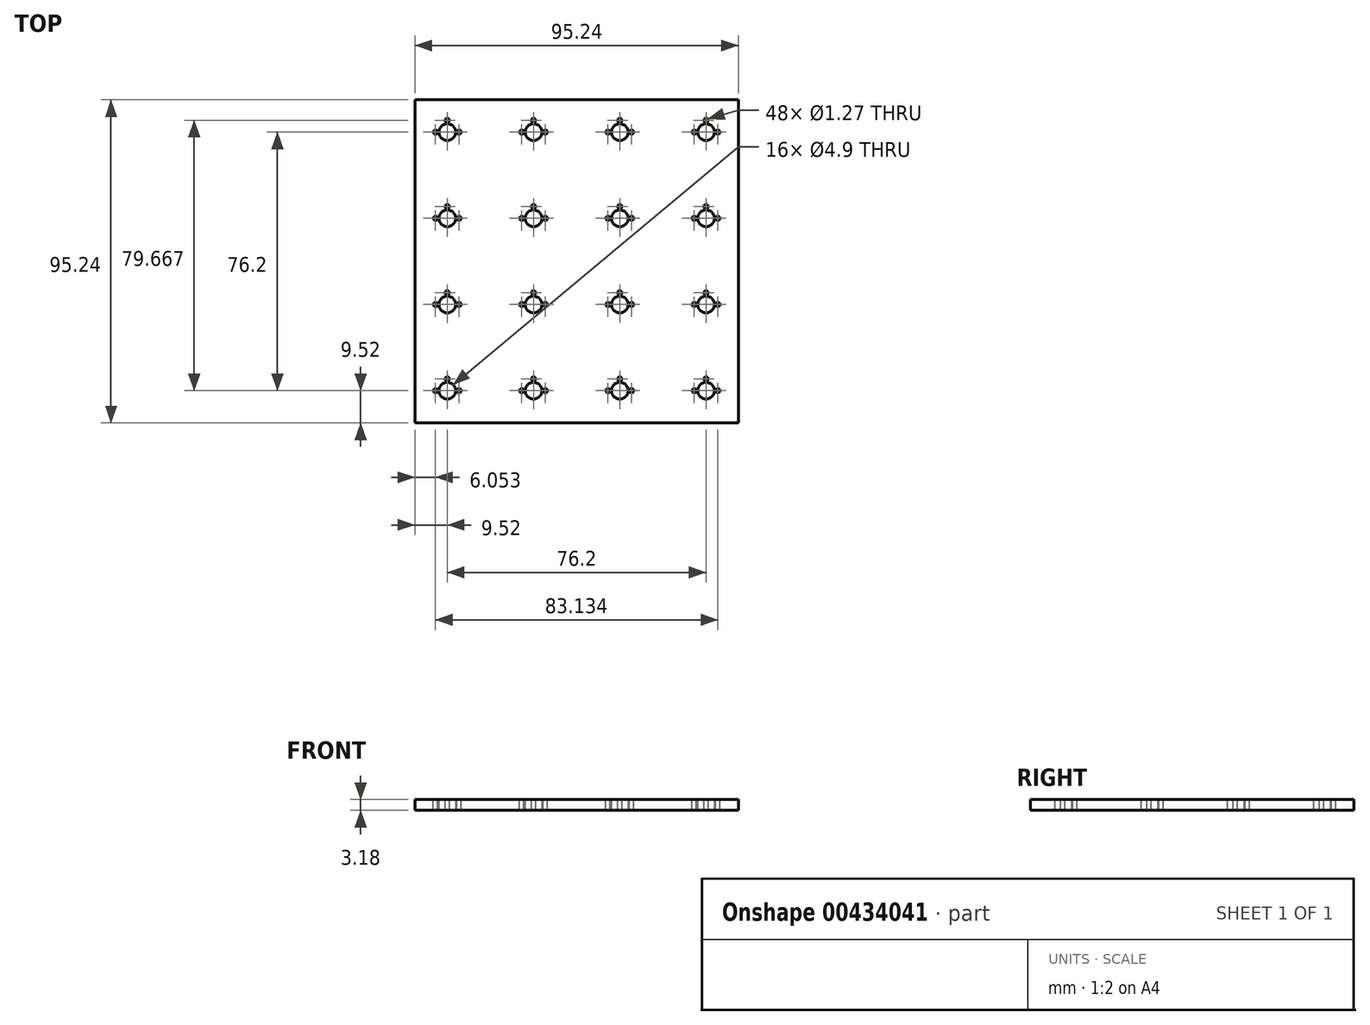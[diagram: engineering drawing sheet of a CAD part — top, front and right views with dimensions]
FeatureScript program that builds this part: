
annotation { "Feature Type Name" : "Feature", "Feature Type Description" : "" }
export const myFeature = defineFeature(function(context is Context, id is Id, definition is map)
    precondition{}
    {
        {
            var Q0;
            Q0=qCreatedBy(makeId("Top.planeOp"),FACE);
            var sketch = newSketch(context, id + "F0", { "sketchPlane" : qUnion([Q0])});
            skLineSegment(sketch, "E0.bottom", {"start": v(47.63, 47.62) * mm, "end": v(-47.62, 47.62) * mm});
            skLineSegment(sketch, "E0.top", {"start": v(47.62, -47.63) * mm, "end": v(-47.63, -47.63) * mm});
            skLineSegment(sketch, "E0.left", {"start": v(47.63, 47.62) * mm, "end": v(47.63, -47.63) * mm});
            skLineSegment(sketch, "E0.right", {"start": v(-47.63, 47.62) * mm, "end": v(-47.63, -47.62) * mm});
            skPoint(sketch, "E0.middle", {"position": v(0, 0) * mm});
            skCircle(sketch, "E1", {"center": v(-38.1, 38.1) * mm, "radius": 2.45 * mm});
            skCircle(sketch, "E2.0.1.0", {"center": v(-38.1, 12.7) * mm, "radius": 2.45 * mm});
            skCircle(sketch, "E2.0.2.0", {"center": v(-38.1, -12.7) * mm, "radius": 2.45 * mm});
            skCircle(sketch, "E2.0.3.0", {"center": v(-38.1, -38.1) * mm, "radius": 2.45 * mm});
            skCircle(sketch, "E2.1.0.0", {"center": v(-12.7, 38.1) * mm, "radius": 2.45 * mm});
            skCircle(sketch, "E2.1.1.0", {"center": v(-12.7, 12.7) * mm, "radius": 2.45 * mm});
            skCircle(sketch, "E2.1.2.0", {"center": v(-12.7, -12.7) * mm, "radius": 2.45 * mm});
            skCircle(sketch, "E2.1.3.0", {"center": v(-12.7, -38.1) * mm, "radius": 2.45 * mm});
            skCircle(sketch, "E2.2.0.0", {"center": v(12.7, 38.1) * mm, "radius": 2.45 * mm});
            skCircle(sketch, "E2.2.1.0", {"center": v(12.7, 12.7) * mm, "radius": 2.45 * mm});
            skCircle(sketch, "E2.2.2.0", {"center": v(12.7, -12.7) * mm, "radius": 2.45 * mm});
            skCircle(sketch, "E2.2.3.0", {"center": v(12.7, -38.1) * mm, "radius": 2.45 * mm});
            skCircle(sketch, "E2.3.0.0", {"center": v(38.1, 38.1) * mm, "radius": 2.45 * mm});
            skCircle(sketch, "E2.3.1.0", {"center": v(38.1, 12.7) * mm, "radius": 2.45 * mm});
            skCircle(sketch, "E2.3.2.0", {"center": v(38.1, -12.7) * mm, "radius": 2.45 * mm});
            skCircle(sketch, "E2.3.3.0", {"center": v(38.1, -38.1) * mm, "radius": 2.45 * mm});
            skLineSegment(sketch, "E2.direction1", {"start": v(-38.1, 38.1) * mm, "end": v(-12.7, 38.1) * mm, "construction": true});
            skLineSegment(sketch, "E2.direction2", {"start": v(-38.1, 38.1) * mm, "end": v(-38.1, 12.7) * mm, "construction": true});
            skSolve(sketch);
        }
        {
            var Q0;
            Q0 = qSketchRegion(id + "F0", true);
            extrude(context, id + "F1", {"entities" : qUnion([Q0]), "depth" : 3.17 * mm});
        }
        {
            var Q0;
            Q0=makeQuery(id+"F1.opExtrude","CAP_FACE",FACE,{"disambiguationData":[OSD([sQuery(id+"F0.wireOp",EDGE,"E0.bottom"),sQuery(id+"F0.wireOp",EDGE,"E0.top"),sQuery(id+"F0.wireOp",EDGE,"E0.left"),sQuery(id+"F0.wireOp",EDGE,"E0.right"),sQuery(id+"F0.wireOp",EDGE,"E1"),sQuery(id+"F0.wireOp",EDGE,"E2.0.1.0"),sQuery(id+"F0.wireOp",EDGE,"E2.0.2.0"),sQuery(id+"F0.wireOp",EDGE,"E2.0.3.0"),sQuery(id+"F0.wireOp",EDGE,"E2.1.0.0"),sQuery(id+"F0.wireOp",EDGE,"E2.1.1.0"),sQuery(id+"F0.wireOp",EDGE,"E2.1.2.0"),sQuery(id+"F0.wireOp",EDGE,"E2.1.3.0"),sQuery(id+"F0.wireOp",EDGE,"E2.2.0.0"),sQuery(id+"F0.wireOp",EDGE,"E2.2.1.0"),sQuery(id+"F0.wireOp",EDGE,"E2.2.2.0"),sQuery(id+"F0.wireOp",EDGE,"E2.2.3.0"),sQuery(id+"F0.wireOp",EDGE,"E2.3.0.0"),sQuery(id+"F0.wireOp",EDGE,"E2.3.1.0"),sQuery(id+"F0.wireOp",EDGE,"E2.3.2.0"),sQuery(id+"F0.wireOp",EDGE,"E2.3.3.0")])],"isStart":false});
            var sketch = newSketch(context, id + "F2", { "sketchPlane" : qUnion([Q0])});
            skCircle(sketch, "E3", {"center": v(-41.57, 38.1) * mm, "radius": 0.64 * mm});
            skCircle(sketch, "E4", {"center": v(-38.1, 41.57) * mm, "radius": 0.64 * mm});
            skCircle(sketch, "E5", {"center": v(-34.63, 38.1) * mm, "radius": 0.64 * mm});
            skLineSegment(sketch, "E6.bottom", {"start": v(-34.63, 41.57) * mm, "end": v(-41.57, 41.57) * mm, "construction": true});
            skLineSegment(sketch, "E6.top", {"start": v(-34.63, 34.63) * mm, "end": v(-41.57, 34.63) * mm, "construction": true});
            skLineSegment(sketch, "E6.left", {"start": v(-34.63, 41.57) * mm, "end": v(-34.63, 34.63) * mm, "construction": true});
            skLineSegment(sketch, "E6.right", {"start": v(-41.57, 41.57) * mm, "end": v(-41.57, 34.63) * mm, "construction": true});
            skPoint(sketch, "E6.middle", {"position": v(-38.1, 38.1) * mm});
            skLineSegment(sketch, "E7", {"start": v(-38.1, 41.57) * mm, "end": v(-38.1, 34.63) * mm, "construction": true});
            skLineSegment(sketch, "E8", {"start": v(-41.57, 38.1) * mm, "end": v(-34.63, 38.1) * mm, "construction": true});
            skPoint(sketch, "E9.0.1.0", {"position": v(-38.1, 12.7) * mm});
            skLineSegment(sketch, "E9.0.1.1", {"start": v(-41.57, 12.7) * mm, "end": v(-34.63, 12.7) * mm, "construction": true});
            skLineSegment(sketch, "E9.0.1.2", {"start": v(-38.1, 16.17) * mm, "end": v(-38.1, 9.23) * mm, "construction": true});
            skLineSegment(sketch, "E9.0.1.3", {"start": v(-34.63, 9.23) * mm, "end": v(-41.57, 9.23) * mm, "construction": true});
            skCircle(sketch, "E9.0.1.4", {"center": v(-41.57, 12.7) * mm, "radius": 0.64 * mm});
            skLineSegment(sketch, "E9.0.1.5", {"start": v(-34.63, 16.17) * mm, "end": v(-34.63, 9.23) * mm, "construction": true});
            skLineSegment(sketch, "E9.0.1.6", {"start": v(-41.57, 16.17) * mm, "end": v(-41.57, 9.23) * mm, "construction": true});
            skCircle(sketch, "E9.0.1.7", {"center": v(-38.1, 16.17) * mm, "radius": 0.64 * mm});
            skLineSegment(sketch, "E9.0.1.8", {"start": v(-34.63, 16.17) * mm, "end": v(-41.57, 16.17) * mm, "construction": true});
            skCircle(sketch, "E9.0.1.9", {"center": v(-34.63, 12.7) * mm, "radius": 0.64 * mm});
            skPoint(sketch, "E9.0.2.0", {"position": v(-38.1, -12.7) * mm});
            skLineSegment(sketch, "E9.0.2.1", {"start": v(-41.57, -12.7) * mm, "end": v(-34.63, -12.7) * mm, "construction": true});
            skLineSegment(sketch, "E9.0.2.2", {"start": v(-38.1, -9.23) * mm, "end": v(-38.1, -16.17) * mm, "construction": true});
            skLineSegment(sketch, "E9.0.2.3", {"start": v(-34.63, -16.17) * mm, "end": v(-41.57, -16.17) * mm, "construction": true});
            skCircle(sketch, "E9.0.2.4", {"center": v(-41.57, -12.7) * mm, "radius": 0.64 * mm});
            skLineSegment(sketch, "E9.0.2.5", {"start": v(-34.63, -9.23) * mm, "end": v(-34.63, -16.17) * mm, "construction": true});
            skLineSegment(sketch, "E9.0.2.6", {"start": v(-41.57, -9.23) * mm, "end": v(-41.57, -16.17) * mm, "construction": true});
            skCircle(sketch, "E9.0.2.7", {"center": v(-38.1, -9.23) * mm, "radius": 0.64 * mm});
            skLineSegment(sketch, "E9.0.2.8", {"start": v(-34.63, -9.23) * mm, "end": v(-41.57, -9.23) * mm, "construction": true});
            skCircle(sketch, "E9.0.2.9", {"center": v(-34.63, -12.7) * mm, "radius": 0.64 * mm});
            skPoint(sketch, "E9.0.3.0", {"position": v(-38.1, -38.1) * mm});
            skLineSegment(sketch, "E9.0.3.1", {"start": v(-41.57, -38.1) * mm, "end": v(-34.63, -38.1) * mm, "construction": true});
            skLineSegment(sketch, "E9.0.3.2", {"start": v(-38.1, -34.63) * mm, "end": v(-38.1, -41.57) * mm, "construction": true});
            skLineSegment(sketch, "E9.0.3.3", {"start": v(-34.63, -41.57) * mm, "end": v(-41.57, -41.57) * mm, "construction": true});
            skCircle(sketch, "E9.0.3.4", {"center": v(-41.57, -38.1) * mm, "radius": 0.64 * mm});
            skLineSegment(sketch, "E9.0.3.5", {"start": v(-34.63, -34.63) * mm, "end": v(-34.63, -41.57) * mm, "construction": true});
            skLineSegment(sketch, "E9.0.3.6", {"start": v(-41.57, -34.63) * mm, "end": v(-41.57, -41.57) * mm, "construction": true});
            skCircle(sketch, "E9.0.3.7", {"center": v(-38.1, -34.63) * mm, "radius": 0.64 * mm});
            skLineSegment(sketch, "E9.0.3.8", {"start": v(-34.63, -34.63) * mm, "end": v(-41.57, -34.63) * mm, "construction": true});
            skCircle(sketch, "E9.0.3.9", {"center": v(-34.63, -38.1) * mm, "radius": 0.64 * mm});
            skPoint(sketch, "E9.1.0.0", {"position": v(-12.7, 38.1) * mm});
            skLineSegment(sketch, "E9.1.0.1", {"start": v(-16.17, 38.1) * mm, "end": v(-9.23, 38.1) * mm, "construction": true});
            skLineSegment(sketch, "E9.1.0.2", {"start": v(-12.7, 41.57) * mm, "end": v(-12.7, 34.63) * mm, "construction": true});
            skLineSegment(sketch, "E9.1.0.3", {"start": v(-9.23, 34.63) * mm, "end": v(-16.17, 34.63) * mm, "construction": true});
            skCircle(sketch, "E9.1.0.4", {"center": v(-16.17, 38.1) * mm, "radius": 0.64 * mm});
            skLineSegment(sketch, "E9.1.0.5", {"start": v(-9.23, 41.57) * mm, "end": v(-9.23, 34.63) * mm, "construction": true});
            skLineSegment(sketch, "E9.1.0.6", {"start": v(-16.17, 41.57) * mm, "end": v(-16.17, 34.63) * mm, "construction": true});
            skCircle(sketch, "E9.1.0.7", {"center": v(-12.7, 41.57) * mm, "radius": 0.64 * mm});
            skLineSegment(sketch, "E9.1.0.8", {"start": v(-9.23, 41.57) * mm, "end": v(-16.17, 41.57) * mm, "construction": true});
            skCircle(sketch, "E9.1.0.9", {"center": v(-9.23, 38.1) * mm, "radius": 0.64 * mm});
            skPoint(sketch, "E9.1.1.0", {"position": v(-12.7, 12.7) * mm});
            skLineSegment(sketch, "E9.1.1.1", {"start": v(-16.17, 12.7) * mm, "end": v(-9.23, 12.7) * mm, "construction": true});
            skLineSegment(sketch, "E9.1.1.2", {"start": v(-12.7, 16.17) * mm, "end": v(-12.7, 9.23) * mm, "construction": true});
            skLineSegment(sketch, "E9.1.1.3", {"start": v(-9.23, 9.23) * mm, "end": v(-16.17, 9.23) * mm, "construction": true});
            skCircle(sketch, "E9.1.1.4", {"center": v(-16.17, 12.7) * mm, "radius": 0.64 * mm});
            skLineSegment(sketch, "E9.1.1.5", {"start": v(-9.23, 16.17) * mm, "end": v(-9.23, 9.23) * mm, "construction": true});
            skLineSegment(sketch, "E9.1.1.6", {"start": v(-16.17, 16.17) * mm, "end": v(-16.17, 9.23) * mm, "construction": true});
            skCircle(sketch, "E9.1.1.7", {"center": v(-12.7, 16.17) * mm, "radius": 0.64 * mm});
            skLineSegment(sketch, "E9.1.1.8", {"start": v(-9.23, 16.17) * mm, "end": v(-16.17, 16.17) * mm, "construction": true});
            skCircle(sketch, "E9.1.1.9", {"center": v(-9.23, 12.7) * mm, "radius": 0.64 * mm});
            skPoint(sketch, "E9.1.2.0", {"position": v(-12.7, -12.7) * mm});
            skLineSegment(sketch, "E9.1.2.1", {"start": v(-16.17, -12.7) * mm, "end": v(-9.23, -12.7) * mm, "construction": true});
            skLineSegment(sketch, "E9.1.2.2", {"start": v(-12.7, -9.23) * mm, "end": v(-12.7, -16.17) * mm, "construction": true});
            skLineSegment(sketch, "E9.1.2.3", {"start": v(-9.23, -16.17) * mm, "end": v(-16.17, -16.17) * mm, "construction": true});
            skCircle(sketch, "E9.1.2.4", {"center": v(-16.17, -12.7) * mm, "radius": 0.64 * mm});
            skLineSegment(sketch, "E9.1.2.5", {"start": v(-9.23, -9.23) * mm, "end": v(-9.23, -16.17) * mm, "construction": true});
            skLineSegment(sketch, "E9.1.2.6", {"start": v(-16.17, -9.23) * mm, "end": v(-16.17, -16.17) * mm, "construction": true});
            skCircle(sketch, "E9.1.2.7", {"center": v(-12.7, -9.23) * mm, "radius": 0.64 * mm});
            skLineSegment(sketch, "E9.1.2.8", {"start": v(-9.23, -9.23) * mm, "end": v(-16.17, -9.23) * mm, "construction": true});
            skCircle(sketch, "E9.1.2.9", {"center": v(-9.23, -12.7) * mm, "radius": 0.64 * mm});
            skPoint(sketch, "E9.1.3.0", {"position": v(-12.7, -38.1) * mm});
            skLineSegment(sketch, "E9.1.3.1", {"start": v(-16.17, -38.1) * mm, "end": v(-9.23, -38.1) * mm, "construction": true});
            skLineSegment(sketch, "E9.1.3.2", {"start": v(-12.7, -34.63) * mm, "end": v(-12.7, -41.57) * mm, "construction": true});
            skLineSegment(sketch, "E9.1.3.3", {"start": v(-9.23, -41.57) * mm, "end": v(-16.17, -41.57) * mm, "construction": true});
            skCircle(sketch, "E9.1.3.4", {"center": v(-16.17, -38.1) * mm, "radius": 0.64 * mm});
            skLineSegment(sketch, "E9.1.3.5", {"start": v(-9.23, -34.63) * mm, "end": v(-9.23, -41.57) * mm, "construction": true});
            skLineSegment(sketch, "E9.1.3.6", {"start": v(-16.17, -34.63) * mm, "end": v(-16.17, -41.57) * mm, "construction": true});
            skCircle(sketch, "E9.1.3.7", {"center": v(-12.7, -34.63) * mm, "radius": 0.64 * mm});
            skLineSegment(sketch, "E9.1.3.8", {"start": v(-9.23, -34.63) * mm, "end": v(-16.17, -34.63) * mm, "construction": true});
            skCircle(sketch, "E9.1.3.9", {"center": v(-9.23, -38.1) * mm, "radius": 0.64 * mm});
            skPoint(sketch, "E9.2.0.0", {"position": v(12.7, 38.1) * mm});
            skLineSegment(sketch, "E9.2.0.1", {"start": v(9.23, 38.1) * mm, "end": v(16.17, 38.1) * mm, "construction": true});
            skLineSegment(sketch, "E9.2.0.2", {"start": v(12.7, 41.57) * mm, "end": v(12.7, 34.63) * mm, "construction": true});
            skLineSegment(sketch, "E9.2.0.3", {"start": v(16.17, 34.63) * mm, "end": v(9.23, 34.63) * mm, "construction": true});
            skCircle(sketch, "E9.2.0.4", {"center": v(9.23, 38.1) * mm, "radius": 0.64 * mm});
            skLineSegment(sketch, "E9.2.0.5", {"start": v(16.17, 41.57) * mm, "end": v(16.17, 34.63) * mm, "construction": true});
            skLineSegment(sketch, "E9.2.0.6", {"start": v(9.23, 41.57) * mm, "end": v(9.23, 34.63) * mm, "construction": true});
            skCircle(sketch, "E9.2.0.7", {"center": v(12.7, 41.57) * mm, "radius": 0.64 * mm});
            skLineSegment(sketch, "E9.2.0.8", {"start": v(16.17, 41.57) * mm, "end": v(9.23, 41.57) * mm, "construction": true});
            skCircle(sketch, "E9.2.0.9", {"center": v(16.17, 38.1) * mm, "radius": 0.64 * mm});
            skPoint(sketch, "E9.2.1.0", {"position": v(12.7, 12.7) * mm});
            skLineSegment(sketch, "E9.2.1.1", {"start": v(9.23, 12.7) * mm, "end": v(16.17, 12.7) * mm, "construction": true});
            skLineSegment(sketch, "E9.2.1.2", {"start": v(12.7, 16.17) * mm, "end": v(12.7, 9.23) * mm, "construction": true});
            skLineSegment(sketch, "E9.2.1.3", {"start": v(16.17, 9.23) * mm, "end": v(9.23, 9.23) * mm, "construction": true});
            skCircle(sketch, "E9.2.1.4", {"center": v(9.23, 12.7) * mm, "radius": 0.64 * mm});
            skLineSegment(sketch, "E9.2.1.5", {"start": v(16.17, 16.17) * mm, "end": v(16.17, 9.23) * mm, "construction": true});
            skLineSegment(sketch, "E9.2.1.6", {"start": v(9.23, 16.17) * mm, "end": v(9.23, 9.23) * mm, "construction": true});
            skCircle(sketch, "E9.2.1.7", {"center": v(12.7, 16.17) * mm, "radius": 0.64 * mm});
            skLineSegment(sketch, "E9.2.1.8", {"start": v(16.17, 16.17) * mm, "end": v(9.23, 16.17) * mm, "construction": true});
            skCircle(sketch, "E9.2.1.9", {"center": v(16.17, 12.7) * mm, "radius": 0.64 * mm});
            skPoint(sketch, "E9.2.2.0", {"position": v(12.7, -12.7) * mm});
            skLineSegment(sketch, "E9.2.2.1", {"start": v(9.23, -12.7) * mm, "end": v(16.17, -12.7) * mm, "construction": true});
            skLineSegment(sketch, "E9.2.2.2", {"start": v(12.7, -9.23) * mm, "end": v(12.7, -16.17) * mm, "construction": true});
            skLineSegment(sketch, "E9.2.2.3", {"start": v(16.17, -16.17) * mm, "end": v(9.23, -16.17) * mm, "construction": true});
            skCircle(sketch, "E9.2.2.4", {"center": v(9.23, -12.7) * mm, "radius": 0.64 * mm});
            skLineSegment(sketch, "E9.2.2.5", {"start": v(16.17, -9.23) * mm, "end": v(16.17, -16.17) * mm, "construction": true});
            skLineSegment(sketch, "E9.2.2.6", {"start": v(9.23, -9.23) * mm, "end": v(9.23, -16.17) * mm, "construction": true});
            skCircle(sketch, "E9.2.2.7", {"center": v(12.7, -9.23) * mm, "radius": 0.64 * mm});
            skLineSegment(sketch, "E9.2.2.8", {"start": v(16.17, -9.23) * mm, "end": v(9.23, -9.23) * mm, "construction": true});
            skCircle(sketch, "E9.2.2.9", {"center": v(16.17, -12.7) * mm, "radius": 0.64 * mm});
            skPoint(sketch, "E9.2.3.0", {"position": v(12.7, -38.1) * mm});
            skLineSegment(sketch, "E9.2.3.1", {"start": v(9.23, -38.1) * mm, "end": v(16.17, -38.1) * mm, "construction": true});
            skLineSegment(sketch, "E9.2.3.2", {"start": v(12.7, -34.63) * mm, "end": v(12.7, -41.57) * mm, "construction": true});
            skLineSegment(sketch, "E9.2.3.3", {"start": v(16.17, -41.57) * mm, "end": v(9.23, -41.57) * mm, "construction": true});
            skCircle(sketch, "E9.2.3.4", {"center": v(9.23, -38.1) * mm, "radius": 0.64 * mm});
            skLineSegment(sketch, "E9.2.3.5", {"start": v(16.17, -34.63) * mm, "end": v(16.17, -41.57) * mm, "construction": true});
            skLineSegment(sketch, "E9.2.3.6", {"start": v(9.23, -34.63) * mm, "end": v(9.23, -41.57) * mm, "construction": true});
            skCircle(sketch, "E9.2.3.7", {"center": v(12.7, -34.63) * mm, "radius": 0.64 * mm});
            skLineSegment(sketch, "E9.2.3.8", {"start": v(16.17, -34.63) * mm, "end": v(9.23, -34.63) * mm, "construction": true});
            skCircle(sketch, "E9.2.3.9", {"center": v(16.17, -38.1) * mm, "radius": 0.64 * mm});
            skPoint(sketch, "E9.3.0.0", {"position": v(38.1, 38.1) * mm});
            skLineSegment(sketch, "E9.3.0.1", {"start": v(34.63, 38.1) * mm, "end": v(41.57, 38.1) * mm, "construction": true});
            skLineSegment(sketch, "E9.3.0.2", {"start": v(38.1, 41.57) * mm, "end": v(38.1, 34.63) * mm, "construction": true});
            skLineSegment(sketch, "E9.3.0.3", {"start": v(41.57, 34.63) * mm, "end": v(34.63, 34.63) * mm, "construction": true});
            skCircle(sketch, "E9.3.0.4", {"center": v(34.63, 38.1) * mm, "radius": 0.64 * mm});
            skLineSegment(sketch, "E9.3.0.5", {"start": v(41.57, 41.57) * mm, "end": v(41.57, 34.63) * mm, "construction": true});
            skLineSegment(sketch, "E9.3.0.6", {"start": v(34.63, 41.57) * mm, "end": v(34.63, 34.63) * mm, "construction": true});
            skCircle(sketch, "E9.3.0.7", {"center": v(38.1, 41.57) * mm, "radius": 0.64 * mm});
            skLineSegment(sketch, "E9.3.0.8", {"start": v(41.57, 41.57) * mm, "end": v(34.63, 41.57) * mm, "construction": true});
            skCircle(sketch, "E9.3.0.9", {"center": v(41.57, 38.1) * mm, "radius": 0.64 * mm});
            skPoint(sketch, "E9.3.1.0", {"position": v(38.1, 12.7) * mm});
            skLineSegment(sketch, "E9.3.1.1", {"start": v(34.63, 12.7) * mm, "end": v(41.57, 12.7) * mm, "construction": true});
            skLineSegment(sketch, "E9.3.1.2", {"start": v(38.1, 16.17) * mm, "end": v(38.1, 9.23) * mm, "construction": true});
            skLineSegment(sketch, "E9.3.1.3", {"start": v(41.57, 9.23) * mm, "end": v(34.63, 9.23) * mm, "construction": true});
            skCircle(sketch, "E9.3.1.4", {"center": v(34.63, 12.7) * mm, "radius": 0.64 * mm});
            skLineSegment(sketch, "E9.3.1.5", {"start": v(41.57, 16.17) * mm, "end": v(41.57, 9.23) * mm, "construction": true});
            skLineSegment(sketch, "E9.3.1.6", {"start": v(34.63, 16.17) * mm, "end": v(34.63, 9.23) * mm, "construction": true});
            skCircle(sketch, "E9.3.1.7", {"center": v(38.1, 16.17) * mm, "radius": 0.64 * mm});
            skLineSegment(sketch, "E9.3.1.8", {"start": v(41.57, 16.17) * mm, "end": v(34.63, 16.17) * mm, "construction": true});
            skCircle(sketch, "E9.3.1.9", {"center": v(41.57, 12.7) * mm, "radius": 0.64 * mm});
            skPoint(sketch, "E9.3.2.0", {"position": v(38.1, -12.7) * mm});
            skLineSegment(sketch, "E9.3.2.1", {"start": v(34.63, -12.7) * mm, "end": v(41.57, -12.7) * mm, "construction": true});
            skLineSegment(sketch, "E9.3.2.2", {"start": v(38.1, -9.23) * mm, "end": v(38.1, -16.17) * mm, "construction": true});
            skLineSegment(sketch, "E9.3.2.3", {"start": v(41.57, -16.17) * mm, "end": v(34.63, -16.17) * mm, "construction": true});
            skCircle(sketch, "E9.3.2.4", {"center": v(34.63, -12.7) * mm, "radius": 0.64 * mm});
            skLineSegment(sketch, "E9.3.2.5", {"start": v(41.57, -9.23) * mm, "end": v(41.57, -16.17) * mm, "construction": true});
            skLineSegment(sketch, "E9.3.2.6", {"start": v(34.63, -9.23) * mm, "end": v(34.63, -16.17) * mm, "construction": true});
            skCircle(sketch, "E9.3.2.7", {"center": v(38.1, -9.23) * mm, "radius": 0.64 * mm});
            skLineSegment(sketch, "E9.3.2.8", {"start": v(41.57, -9.23) * mm, "end": v(34.63, -9.23) * mm, "construction": true});
            skCircle(sketch, "E9.3.2.9", {"center": v(41.57, -12.7) * mm, "radius": 0.64 * mm});
            skPoint(sketch, "E9.3.3.0", {"position": v(38.1, -38.1) * mm});
            skLineSegment(sketch, "E9.3.3.1", {"start": v(34.63, -38.1) * mm, "end": v(41.57, -38.1) * mm, "construction": true});
            skLineSegment(sketch, "E9.3.3.2", {"start": v(38.1, -34.63) * mm, "end": v(38.1, -41.57) * mm, "construction": true});
            skLineSegment(sketch, "E9.3.3.3", {"start": v(41.57, -41.57) * mm, "end": v(34.63, -41.57) * mm, "construction": true});
            skCircle(sketch, "E9.3.3.4", {"center": v(34.63, -38.1) * mm, "radius": 0.64 * mm});
            skLineSegment(sketch, "E9.3.3.5", {"start": v(41.57, -34.63) * mm, "end": v(41.57, -41.57) * mm, "construction": true});
            skLineSegment(sketch, "E9.3.3.6", {"start": v(34.63, -34.63) * mm, "end": v(34.63, -41.57) * mm, "construction": true});
            skCircle(sketch, "E9.3.3.7", {"center": v(38.1, -34.63) * mm, "radius": 0.64 * mm});
            skLineSegment(sketch, "E9.3.3.8", {"start": v(41.57, -34.63) * mm, "end": v(34.63, -34.63) * mm, "construction": true});
            skCircle(sketch, "E9.3.3.9", {"center": v(41.57, -38.1) * mm, "radius": 0.64 * mm});
            skLineSegment(sketch, "E9.direction1", {"start": v(-41.57, 34.63) * mm, "end": v(-16.17, 34.63) * mm, "construction": true});
            skLineSegment(sketch, "E9.direction2", {"start": v(-41.57, 34.63) * mm, "end": v(-41.57, 9.23) * mm, "construction": true});
            skSolve(sketch);
        }
        {
            var Q0;
            Q0 = qSketchRegion(id + "F2", true);
            extrude(context, id + "F3", {"entities" : qUnion([Q0]), "operationType" : NewBodyOperationType.REMOVE, "oppositeDirection" : true, "depth" : 5.08 * mm});
        }
    });
